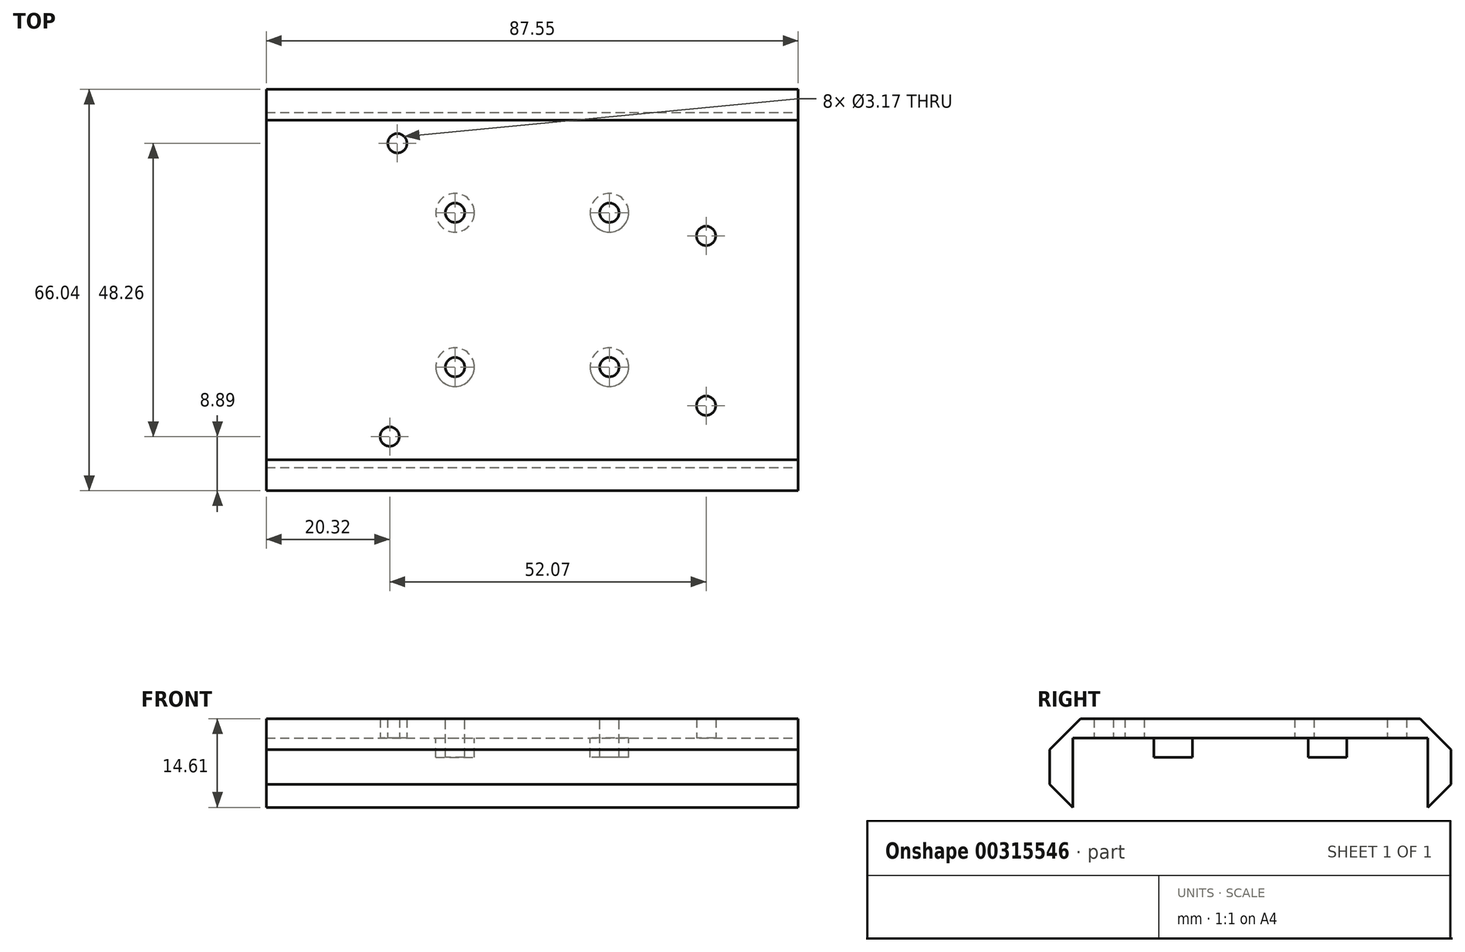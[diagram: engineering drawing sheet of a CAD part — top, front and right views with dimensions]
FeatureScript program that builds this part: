
annotation { "Feature Type Name" : "Feature", "Feature Type Description" : "" }
export const myFeature = defineFeature(function(context is Context, id is Id, definition is map)
    precondition{}
    {
        {
            var Q0;
            Q0=qCreatedBy(makeId("Top.planeOp"),FACE);
            var sketch = newSketch(context, id + "F0", { "sketchPlane" : qUnion([Q0])});
            skCircle(sketch, "E0", {"center": v(0, 0) * mm, "radius": 1.59 * mm});
            skCircle(sketch, "E1", {"center": v(50.8, -15.24) * mm, "radius": 1.59 * mm});
            skCircle(sketch, "E2", {"center": v(50.8, -43.18) * mm, "radius": 1.59 * mm});
            skCircle(sketch, "E3", {"center": v(-1.27, -48.26) * mm, "radius": 1.59 * mm});
            skLineSegment(sketch, "E4.0", {"start": v(-21.6, 8.9) * mm, "end": v(-21.59, -57.15) * mm});
            skLineSegment(sketch, "E4.1", {"start": v(-21.6, 8.9) * mm, "end": v(65.96, 8.9) * mm});
            skLineSegment(sketch, "E4.2", {"start": v(65.96, 8.9) * mm, "end": v(65.96, -57.15) * mm});
            skLineSegment(sketch, "E4.3", {"start": v(-21.6, -57.15) * mm, "end": v(65.96, -57.15) * mm});
            skSolve(sketch);
        }
        {
            var Q0;
            Q0=makeQuery(id+"F0.imprint","IMPRINT",FACE,{"disambiguationData":[TD([[makeQuery(id+"F0.imprint","IMPRINT",EDGE,{"derivedFrom":sQuery(id+"F0.wireOp",EDGE,"E0")}),-1.0]])]});
            extrude(context, id + "F1", {"entities" : qUnion([Q0]), "depth" : 3.17 * mm});
        }
        {
            var Q0;
            Q0=makeQuery(id+"F1.opExtrude","CAP_FACE",FACE,{"disambiguationData":[OSD([sQuery(id+"F0.wireOp",EDGE,"E0"),sQuery(id+"F0.wireOp",EDGE,"E1"),sQuery(id+"F0.wireOp",EDGE,"E2"),sQuery(id+"F0.wireOp",EDGE,"E3"),sQuery(id+"F0.wireOp",EDGE,"E4.0"),sQuery(id+"F0.wireOp",EDGE,"E4.1"),sQuery(id+"F0.wireOp",EDGE,"E4.2"),sQuery(id+"F0.wireOp",EDGE,"E4.3")])],"isStart":true});
            var sketch = newSketch(context, id + "F2", { "sketchPlane" : qUnion([Q0])});
            skPoint(sketch, "E5.middle", {"position": v(22.18, 24.13) * mm});
            skPoint(sketch, "E5.middle.positionSnap0", {"position": v(22.18, -8.9) * mm});
            skPoint(sketch, "E5.middle.positionSnap1", {"position": v(65.96, 24.13) * mm});
            skPoint(sketch, "E5.centerSnap0", {"position": v(22.18, -8.9) * mm});
            skPoint(sketch, "E5.centerSnap1", {"position": v(65.96, 24.13) * mm});
            skCircle(sketch, "E6", {"center": v(9.48, 11.43) * mm, "radius": 1.59 * mm});
            skCircle(sketch, "E7", {"center": v(9.48, 36.83) * mm, "radius": 1.59 * mm});
            skCircle(sketch, "E8", {"center": v(34.88, 36.83) * mm, "radius": 1.59 * mm});
            skCircle(sketch, "E9", {"center": v(34.88, 11.43) * mm, "radius": 1.59 * mm});
            skCircle(sketch, "E10", {"center": v(9.48, 11.43) * mm, "radius": 3.18 * mm});
            skCircle(sketch, "E11", {"center": v(9.48, 36.83) * mm, "radius": 3.18 * mm});
            skCircle(sketch, "E12", {"center": v(34.88, 36.83) * mm, "radius": 3.18 * mm});
            skCircle(sketch, "E13", {"center": v(34.88, 11.43) * mm, "radius": 3.18 * mm});
            skSolve(sketch);
        }
        {
            var Q0;
            Q0=makeQuery(id+"F2.imprint","IMPRINT",FACE,{"disambiguationData":[TD([[makeQuery(id+"F2.imprint","IMPRINT",EDGE,{"derivedFrom":sQuery(id+"F2.wireOp",EDGE,"E6")}),-1.0]])]});
            var Q1;
            Q1=makeQuery(id+"F2.imprint","IMPRINT",FACE,{"disambiguationData":[TD([[makeQuery(id+"F2.imprint","IMPRINT",EDGE,{"derivedFrom":sQuery(id+"F2.wireOp",EDGE,"E7")}),-1.0]])]});
            var Q2;
            Q2=makeQuery(id+"F2.imprint","IMPRINT",FACE,{"disambiguationData":[TD([[makeQuery(id+"F2.imprint","IMPRINT",EDGE,{"derivedFrom":sQuery(id+"F2.wireOp",EDGE,"E8")}),-1.0]])]});
            var Q3;
            Q3=makeQuery(id+"F2.imprint","IMPRINT",FACE,{"disambiguationData":[TD([[makeQuery(id+"F2.imprint","IMPRINT",EDGE,{"derivedFrom":sQuery(id+"F2.wireOp",EDGE,"E9")}),-1.0]])]});
            extrude(context, id + "F3", {"entities" : qUnion([Q0, Q1, Q2, Q3]), "operationType" : NewBodyOperationType.ADD, "depth" : 3.17 * mm});
        }
        {
            var Q0;
            Q0=makeQuery(id+"F3.boolean.opBoolean","SPLIT",FACE,{"disambiguationData":[TD([makeQuery(id+"F3.opExtrude","SWEPT_FACE",FACE,{"disambiguationData":[OSD([sQuery(id+"F2.wireOp",EDGE,"E6")])]})])],"derivedFrom":makeQuery(id+"F1.opExtrude","CAP_FACE",FACE,{"disambiguationData":[OSD([sQuery(id+"F0.wireOp",EDGE,"E0"),sQuery(id+"F0.wireOp",EDGE,"E1"),sQuery(id+"F0.wireOp",EDGE,"E2"),sQuery(id+"F0.wireOp",EDGE,"E3"),sQuery(id+"F0.wireOp",EDGE,"E4.0"),sQuery(id+"F0.wireOp",EDGE,"E4.1"),sQuery(id+"F0.wireOp",EDGE,"E4.2"),sQuery(id+"F0.wireOp",EDGE,"E4.3")])],"isStart":true})});
            var Q1;
            Q1=makeQuery(id+"F3.boolean.opBoolean","SPLIT",FACE,{"disambiguationData":[TD([makeQuery(id+"F3.opExtrude","SWEPT_FACE",FACE,{"disambiguationData":[OSD([sQuery(id+"F2.wireOp",EDGE,"E7")])]})])],"derivedFrom":makeQuery(id+"F1.opExtrude","CAP_FACE",FACE,{"disambiguationData":[OSD([sQuery(id+"F0.wireOp",EDGE,"E0"),sQuery(id+"F0.wireOp",EDGE,"E1"),sQuery(id+"F0.wireOp",EDGE,"E2"),sQuery(id+"F0.wireOp",EDGE,"E3"),sQuery(id+"F0.wireOp",EDGE,"E4.0"),sQuery(id+"F0.wireOp",EDGE,"E4.1"),sQuery(id+"F0.wireOp",EDGE,"E4.2"),sQuery(id+"F0.wireOp",EDGE,"E4.3")])],"isStart":true})});
            var Q2;
            Q2=makeQuery(id+"F3.boolean.opBoolean","SPLIT",FACE,{"disambiguationData":[TD([makeQuery(id+"F3.opExtrude","SWEPT_FACE",FACE,{"disambiguationData":[OSD([sQuery(id+"F2.wireOp",EDGE,"E8")])]})])],"derivedFrom":makeQuery(id+"F1.opExtrude","CAP_FACE",FACE,{"disambiguationData":[OSD([sQuery(id+"F0.wireOp",EDGE,"E0"),sQuery(id+"F0.wireOp",EDGE,"E1"),sQuery(id+"F0.wireOp",EDGE,"E2"),sQuery(id+"F0.wireOp",EDGE,"E3"),sQuery(id+"F0.wireOp",EDGE,"E4.0"),sQuery(id+"F0.wireOp",EDGE,"E4.1"),sQuery(id+"F0.wireOp",EDGE,"E4.2"),sQuery(id+"F0.wireOp",EDGE,"E4.3")])],"isStart":true})});
            var Q3;
            Q3=makeQuery(id+"F3.boolean.opBoolean","SPLIT",FACE,{"disambiguationData":[TD([makeQuery(id+"F3.opExtrude","SWEPT_FACE",FACE,{"disambiguationData":[OSD([sQuery(id+"F2.wireOp",EDGE,"E9")])]})])],"derivedFrom":makeQuery(id+"F1.opExtrude","CAP_FACE",FACE,{"disambiguationData":[OSD([sQuery(id+"F0.wireOp",EDGE,"E0"),sQuery(id+"F0.wireOp",EDGE,"E1"),sQuery(id+"F0.wireOp",EDGE,"E2"),sQuery(id+"F0.wireOp",EDGE,"E3"),sQuery(id+"F0.wireOp",EDGE,"E4.0"),sQuery(id+"F0.wireOp",EDGE,"E4.1"),sQuery(id+"F0.wireOp",EDGE,"E4.2"),sQuery(id+"F0.wireOp",EDGE,"E4.3")])],"isStart":true})});
            extrude(context, id + "F4", {"entities" : qUnion([Q0, Q1, Q2, Q3]), "operationType" : NewBodyOperationType.REMOVE, "oppositeDirection" : true, "depth" : 25.4 * mm});
        }
        {
            var Q0;
            {var subQ0=sQuery(id+"F0.wireOp",EDGE,"E4.3");var subQ1=sQuery(id+"F0.wireOp",EDGE,"E4.2");var subQ2=sQuery(id+"F0.wireOp",EDGE,"E4.1");var subQ3=sQuery(id+"F0.wireOp",EDGE,"E4.0");var subQ4=sQuery(id+"F0.wireOp",EDGE,"E0");var subQ5=sQuery(id+"F0.wireOp",EDGE,"E3");var subQ6=sQuery(id+"F0.wireOp",EDGE,"E1");var subQ7=sQuery(id+"F0.wireOp",EDGE,"E2");Q0=makeQuery(id+"F3.boolean.opBoolean","SPLIT",FACE,{"disambiguationData":[TD([makeQuery(id+"F1.opExtrude","SWEPT_FACE",FACE,{"disambiguationData":[OSD([subQ4])]})])],"derivedFrom":makeQuery(id+"F1.opExtrude","CAP_FACE",FACE,{"disambiguationData":[OSD([subQ4,subQ6,subQ7,subQ5,subQ3,subQ2,subQ1,subQ0])],"isStart":true})});}
            var sketch = newSketch(context, id + "F5", { "sketchPlane" : qUnion([Q0])});
            skLineSegment(sketch, "E14.bottom", {"start": v(-21.59, 57.15) * mm, "end": v(65.96, 57.15) * mm});
            skLineSegment(sketch, "E14.top", {"start": v(-21.59, 53.34) * mm, "end": v(65.96, 53.34) * mm});
            skLineSegment(sketch, "E14.left", {"start": v(-21.59, 57.15) * mm, "end": v(-21.59, 53.34) * mm});
            skLineSegment(sketch, "E14.right", {"start": v(65.96, 57.15) * mm, "end": v(65.96, 53.34) * mm});
            skLineSegment(sketch, "E15.bottom", {"start": v(-21.6, -8.9) * mm, "end": v(65.96, -8.9) * mm});
            skLineSegment(sketch, "E15.top", {"start": v(-21.6, -5.08) * mm, "end": v(65.96, -5.08) * mm});
            skLineSegment(sketch, "E15.left", {"start": v(-21.6, -8.9) * mm, "end": v(-21.6, -5.08) * mm});
            skLineSegment(sketch, "E15.right", {"start": v(65.96, -8.9) * mm, "end": v(65.96, -5.08) * mm});
            skSolve(sketch);
        }
        {
            var Q0;
            Q0=makeQuery(id+"F5.imprint","IMPRINT",FACE,{"disambiguationData":[TD([[makeQuery(id+"F5.imprint","IMPRINT",EDGE,{"derivedFrom":sQuery(id+"F5.wireOp",EDGE,"E15.bottom")}),1.0]])]});
            var Q1;
            Q1=makeQuery(id+"F5.imprint","IMPRINT",FACE,{"disambiguationData":[TD([[makeQuery(id+"F5.imprint","IMPRINT",EDGE,{"derivedFrom":sQuery(id+"F5.wireOp",EDGE,"E14.bottom")}),-1.0]])]});
            extrude(context, id + "F6", {"entities" : qUnion([Q0, Q1]), "operationType" : NewBodyOperationType.ADD, "depth" : 12.7 * mm});
        }
        {
            var Q0;
            Q0=makeQuery(id+"F1.opExtrude","CAP_EDGE",EDGE,{"disambiguationData":[OSD([sQuery(id+"F0.wireOp",EDGE,"E4.1")])],"isStart":false});
            var Q1;
            Q1=makeQuery(id+"F1.opExtrude","CAP_EDGE",EDGE,{"disambiguationData":[OSD([sQuery(id+"F0.wireOp",EDGE,"E4.3")])],"isStart":false});
            var Q2;
            Q2=makeQuery(id+"F6.opExtrude","CAP_EDGE",EDGE,{"disambiguationData":[OSD([sQuery(id+"F5.wireOp",EDGE,"E15.bottom")])],"isStart":false});
            var Q3;
            Q3=makeQuery(id+"F6.opExtrude","CAP_EDGE",EDGE,{"disambiguationData":[OSD([sQuery(id+"F5.wireOp",EDGE,"E14.bottom")])],"isStart":false});
            chamfer(context, id + "F7", {"entities" : qUnion([Q0, Q1, Q2, Q3]), "width" : 5.08 * mm, "tangentPropagation" : true});
        }
    });
